# Revit family: BD-40_SO13025
name_source: partatom
category: Aparatos eléctricos
revit_build: Autodesk Revit 2016 (Build: 20150220_1215(x64)
units: mm (PartAtom-declared; Revit-internal decimal feet)

## family parameters
Compartido = No
Corte con vacíos al cargar = No
Cota de conector redondo = Diámetro de uso
Mantener orientación de anotación = No
Número OmniClass = 23.80.00.00
Punto de cálculo de habitación = No
Se basa en plano de trabajo = No
Siempre vertical = Sí
Tipo de pieza = Caja de conexiones
Título OmniClass = Electric Power and Lighting

## types (1)
- Disipadores dinamicos
    Caudal agua = 3000 l/h
    Colector = 50 m2
    Costo = 0 $
    Código de montaje = SO13025
    Descripción = DISIPADORES DINÁMICOS BD
    Dimensiones = 800x690x250 mm
    Fabricante = SALVADOR ESCODA
    Imagen de tipo = disipadores_BD40-400.jpg
    Modelo = BD 40
    Motor (220V II) = 140x2 W
    Nº ventiladores = 2
    P.C.A Agua = 1,19 m.c.a.
    P.C.A Aire = 109 Pa
    Potencia disipación = 40 kW
    Tª entrada agua = 90 ºC
    Tª entrada aire = 35 ºC
    Tª salida agua = 77,60 ºC
    Tª salida aire = 69 ºC
    URL = www.salvadorescoda.com
